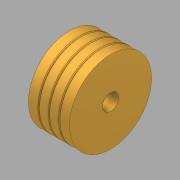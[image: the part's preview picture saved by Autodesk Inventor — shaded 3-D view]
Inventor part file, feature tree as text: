
AUTODESK INVENTOR PART (.ipt)
format: ipt  version: 2020 (Build 240168000, 168)  size: 128,512 bytes
history: native  units: in
note: dims shown in document units (in); Inventor stores cm internally (conversion verified against a paired STEP export)
features: sketch x2, other x1, revolve x1, hole x1
ambient origin geometry x8: Origin, YZ Plane, XZ Plane, XY Plane, X Axis, Y Axis, Z Axis, Center Point
bodies: Body1 (feature_tree)
feature tree (5):
  other  "Sólido1"
  revolve  "Revolución1"  [1 undecoded]
  hole  "Agujero1"  [1 undecoded]
  sketch  "Boceto1"  dims[d0=0.25in d1=0.25in]
  sketch  "Boceto2"  dims[d3=0.0625in d6=0.0625in d7=0.0625in d12=90.0deg d13=0.0764in d14=0.25in d15=0.099in d16=0.125in d17=0.5635in d18=0.302in d19=0.8108in]
note: 2 required parameter values undecoded (feature->parameter linkage not recoverable at this tier; creation-order binding heuristic only, values carry confidence <= 0.55)